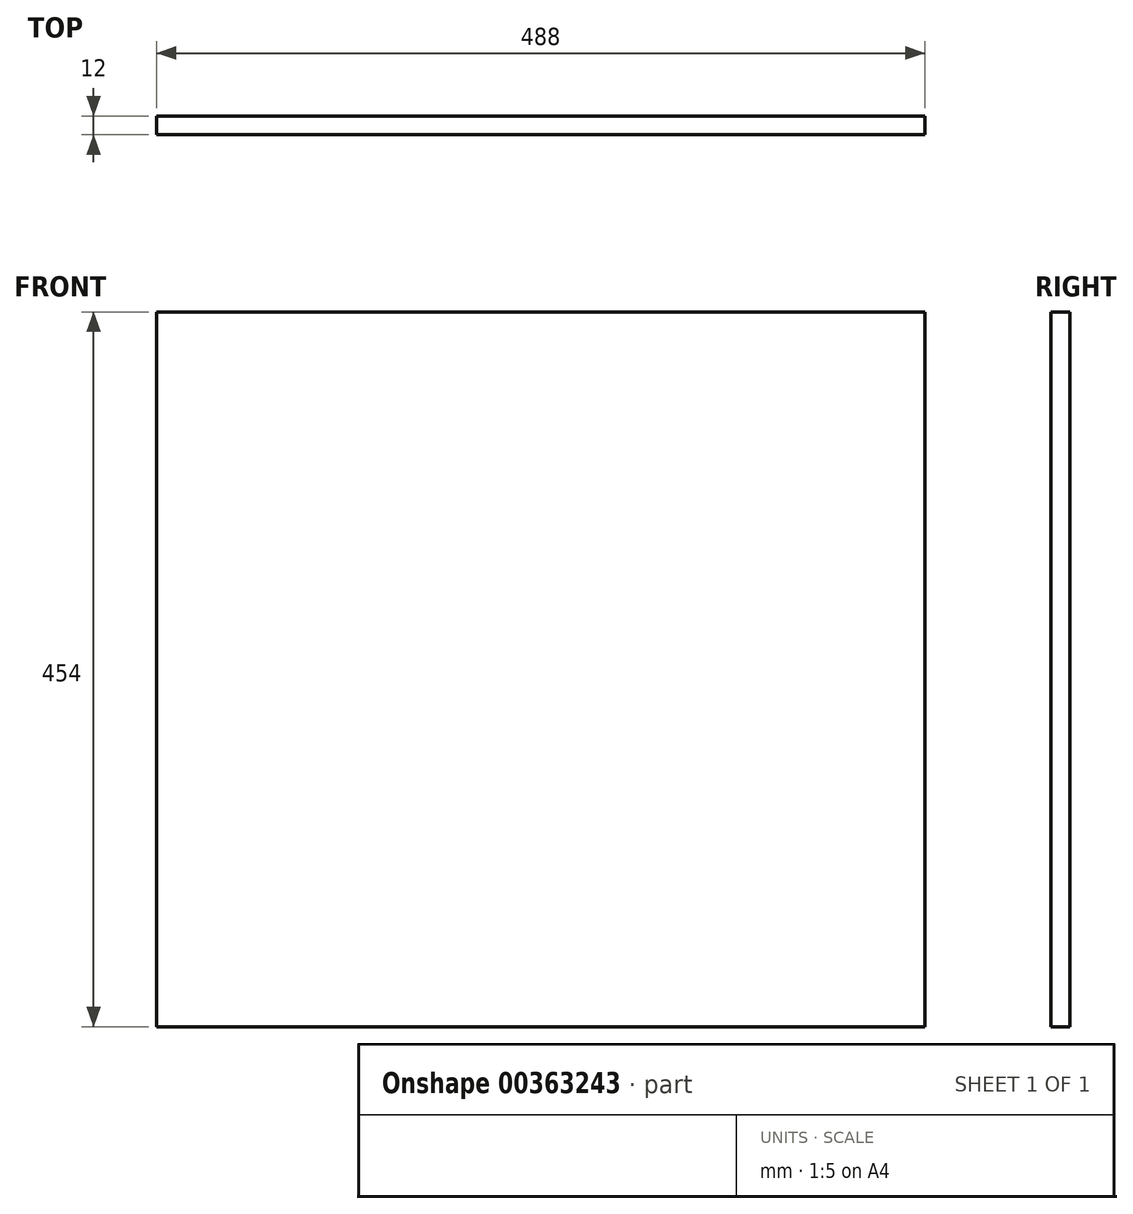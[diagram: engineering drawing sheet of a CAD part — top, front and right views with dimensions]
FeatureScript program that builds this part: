
annotation { "Feature Type Name" : "Feature", "Feature Type Description" : "" }
export const myFeature = defineFeature(function(context is Context, id is Id, definition is map)
    precondition{}
    {
        {
            assignVariable(context, id + "F0", {"name" : "thickness", "anyValue" : 12});
        }
        {
            var Q0;
            Q0=qCreatedBy(makeId("Front.planeOp"),FACE);
            var sketch = newSketch(context, id + "F1", { "sketchPlane" : qUnion([Q0])});
            skLineSegment(sketch, "E0.bottom", {"start": v(244, 227) * mm, "end": v(-244, 227) * mm});
            skLineSegment(sketch, "E0.top", {"start": v(244, -227) * mm, "end": v(-244, -227) * mm});
            skLineSegment(sketch, "E0.left", {"start": v(244, 227) * mm, "end": v(244, -227) * mm});
            skLineSegment(sketch, "E0.right", {"start": v(-244, 227) * mm, "end": v(-244, -227) * mm});
            skPoint(sketch, "E0.middle", {"position": v(0, 0) * mm});
            skSolve(sketch);
        }
        {
            var Q0;
            Q0=makeQuery(id+"F1.imprint","IMPRINT",FACE,{"disambiguationData":[TD([[makeQuery(id+"F1.imprint","IMPRINT",EDGE,{"derivedFrom":sQuery(id+"F1.wireOp",EDGE,"E0.bottom")}),1.0]])]});
            extrude(context, id + "F2", {"entities" : qUnion([Q0]), "depth" : (getVariable(context, 'thickness')) * mm});
        }
    });
